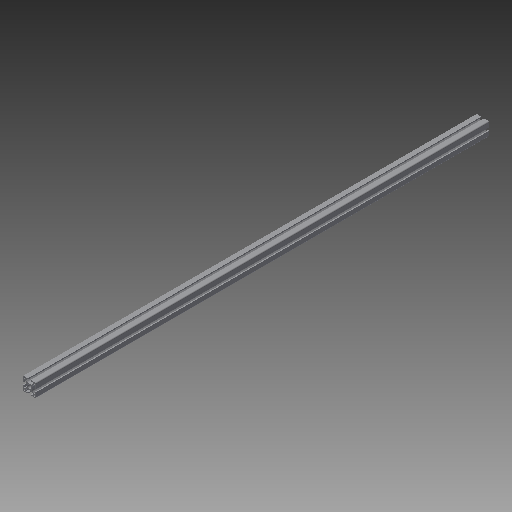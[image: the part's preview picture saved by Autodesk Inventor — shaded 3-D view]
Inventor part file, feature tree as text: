
AUTODESK INVENTOR PART (.ipt)
format: ipt  version: 2018 (Build 220112000, 112)  size: 221,696 bytes
history: native  units: mm
features: other x42, sketch x5, hole x4, extrude x1
ambient origin geometry x8: Origin, YZ Plane, XZ Plane, XY Plane, X Axis, Y Axis, Z Axis, Center Point
bodies: Solid1 (feature_tree)
feature tree (52):
  extrude  "Extrusion1"  [1 undecoded]
  hole  "Drilling 1"  [1 undecoded]
  hole  "Drilling 2"  [1 undecoded]
  hole  "Drilling 3"  [1 undecoded]
  hole  "Drilling 4"  [1 undecoded]
  other  "side_4d_XY"
  other  "side_4d_YZ"
  other  "side_4d_ZX"
  other  "side_4d_X"
  other  "side_4d_Y"
  other  "side_4d_Z"
  other  "side_4d_Center"
  other  "side_1a_XY"
  other  "side_1a_YZ"
  other  "side_1a_ZX"
  other  "side_1a_X"
  other  "side_1a_Y"
  other  "side_1a_Z"
  other  "side_1a_Center"
  other  "side_2b_XY"
  other  "side_2b_YZ"
  other  "side_2b_ZX"
  other  "side_2b_X"
  other  "side_2b_Y"
  other  "side_2b_Z"
  other  "side_2b_Center"
  other  "side_3c_XY"
  other  "side_3c_YZ"
  other  "side_3c_ZX"
  other  "side_3c_X"
  other  "side_3c_Y"
  other  "side_3c_Z"
  other  "side_3c_Center"
  other  "end_XY"
  other  "end_YZ"
  other  "end_ZX"
  other  "end_X"
  other  "end_Y"
  other  "end_Z"
  other  "end_Center"
  other  "start_XY"
  other  "start_YZ"
  other  "start_ZX"
  other  "start_X"
  other  "start_Y"
  other  "start_Z"
  other  "start_Center"
  sketch  "Skizze_1"  dims[d0=1360.0mm d1=0.0mm]
  sketch  "Sketch2"  dims[d2=5.0mm d3=6.0mm d4=4.0mm d5=2.0mm d6=90.0deg d7=6000.0mm d8=0.0mm]
  sketch  "Sketch3"  dims[d9=5.0mm d10=6.0mm d11=4.0mm d12=2.0mm d13=90.0deg d14=6000.0mm d15=0.0mm]
  sketch  "Sketch4"  dims[d16=5.0mm d17=6.0mm d18=4.0mm d19=2.0mm d20=90.0deg d21=6000.0mm d22=0.0mm]
  sketch  "Sketch5"  dims[d23=5.0mm d24=6.0mm d25=4.0mm d26=2.0mm d27=90.0deg d28=6000.0mm d29=0.0mm]
note: 5 required parameter values undecoded (feature->parameter linkage not recoverable at this tier; creation-order binding heuristic only, values carry confidence <= 0.55)
